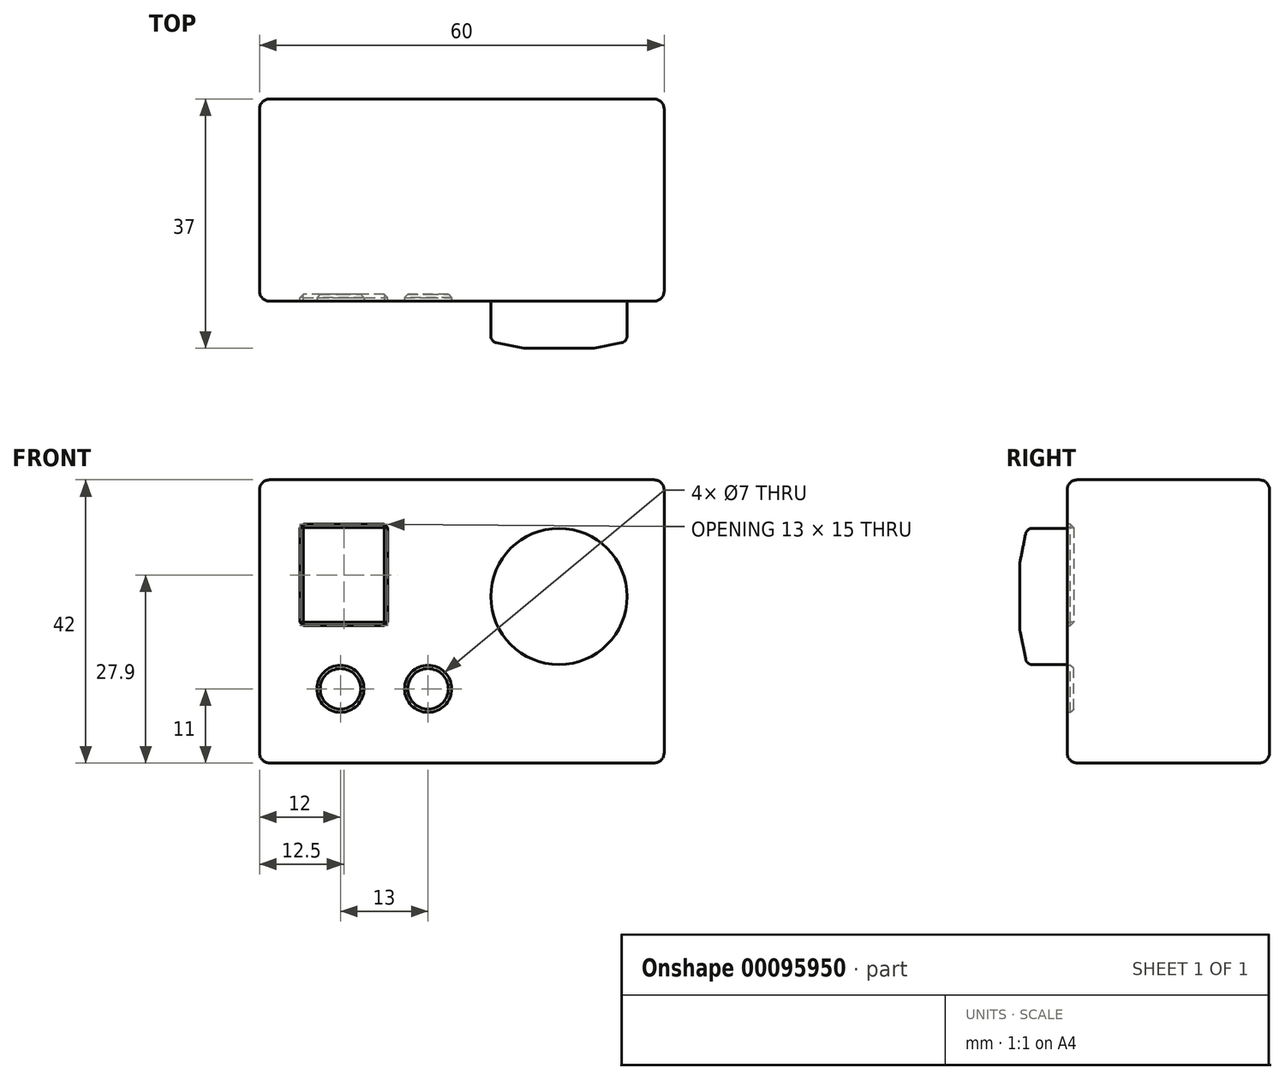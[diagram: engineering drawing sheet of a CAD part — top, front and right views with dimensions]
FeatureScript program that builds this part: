
annotation { "Feature Type Name" : "Feature", "Feature Type Description" : "" }
export const myFeature = defineFeature(function(context is Context, id is Id, definition is map)
    precondition{}
    {
        {
            var Q0;
            Q0=qCreatedBy(makeId("Front.planeOp"),FACE);
            var sketch = newSketch(context, id + "F0", { "sketchPlane" : qUnion([Q0])});
            skLineSegment(sketch, "E0.bottom", {"start": v(30, 21) * mm, "end": v(-30, 21) * mm});
            skLineSegment(sketch, "E0.top", {"start": v(30, -21) * mm, "end": v(-30, -21) * mm});
            skLineSegment(sketch, "E0.left", {"start": v(30, 21) * mm, "end": v(30, -21) * mm});
            skLineSegment(sketch, "E0.right", {"start": v(-30, 21) * mm, "end": v(-30, -21) * mm});
            skPoint(sketch, "E0.middle", {"position": v(0, 0) * mm});
            skSolve(sketch);
        }
        {
            var Q0;
            Q0 = qSketchRegion(id + "F0", true);
            extrude(context, id + "F1", {"entities" : qUnion([Q0]), "depth" : 30 * mm});
        }
        {
            var Q0;
            Q0=makeQuery(id+"F1.opExtrude","CAP_FACE",FACE,{"disambiguationData":[OSD([sQuery(id+"F0.wireOp",EDGE,"E0.bottom"),sQuery(id+"F0.wireOp",EDGE,"E0.top"),sQuery(id+"F0.wireOp",EDGE,"E0.left"),sQuery(id+"F0.wireOp",EDGE,"E0.right")])],"isStart":false});
            var sketch = newSketch(context, id + "F2", { "sketchPlane" : qUnion([Q0])});
            skCircle(sketch, "E1", {"center": v(-18, -10) * mm, "radius": 3.5 * mm});
            skCircle(sketch, "E2", {"center": v(-5, -10) * mm, "radius": 3.5 * mm});
            skLineSegment(sketch, "E3.bottom", {"start": v(-24, 14.4) * mm, "end": v(-11, 14.4) * mm});
            skLineSegment(sketch, "E3.top", {"start": v(-24, -0.6) * mm, "end": v(-11, -0.6) * mm});
            skLineSegment(sketch, "E3.left", {"start": v(-24, 14.4) * mm, "end": v(-24, -0.6) * mm});
            skLineSegment(sketch, "E3.right", {"start": v(-11, 14.4) * mm, "end": v(-11, -0.6) * mm});
            skSolve(sketch);
        }
        {
            var Q0;
            Q0 = qSketchRegion(id + "F2", true);
            extrude(context, id + "F3", {"entities" : qUnion([Q0]), "operationType" : NewBodyOperationType.REMOVE, "oppositeDirection" : true, "depth" : 1 * mm});
        }
        {
            var Q0;
            Q0=makeQuery(id+"F3.boolean.opBoolean","COPY",EDGE,{"derivedFrom":makeQuery(id+"F3.opExtrude","CAP_EDGE",EDGE,{"disambiguationData":[OSD([sQuery(id+"F2.wireOp",EDGE,"E1")])],"isStart":true})});
            var Q1;
            Q1=makeQuery(id+"F3.boolean.opBoolean","COPY",EDGE,{"derivedFrom":makeQuery(id+"F3.opExtrude","CAP_EDGE",EDGE,{"disambiguationData":[OSD([sQuery(id+"F2.wireOp",EDGE,"E2")])],"isStart":true})});
            var Q2;
            Q2=makeQuery(id+"F3.boolean.opBoolean","COPY",EDGE,{"derivedFrom":makeQuery(id+"F3.opExtrude","CAP_EDGE",EDGE,{"disambiguationData":[OSD([sQuery(id+"F2.wireOp",EDGE,"E3.right")])],"isStart":true})});
            var Q3;
            Q3=makeQuery(id+"F3.boolean.opBoolean","COPY",EDGE,{"derivedFrom":makeQuery(id+"F3.opExtrude","CAP_EDGE",EDGE,{"disambiguationData":[OSD([sQuery(id+"F2.wireOp",EDGE,"E1")])],"isStart":false})});
            var Q4;
            Q4=makeQuery(id+"F3.boolean.opBoolean","COPY",EDGE,{"derivedFrom":makeQuery(id+"F3.opExtrude","CAP_EDGE",EDGE,{"disambiguationData":[OSD([sQuery(id+"F2.wireOp",EDGE,"E2")])],"isStart":false})});
            var Q5;
            Q5=makeQuery(id+"F3.boolean.opBoolean","COPY",EDGE,{"derivedFrom":makeQuery(id+"F3.opExtrude","CAP_EDGE",EDGE,{"disambiguationData":[OSD([sQuery(id+"F2.wireOp",EDGE,"E3.bottom")])],"isStart":true})});
            var Q6;
            Q6=makeQuery(id+"F3.boolean.opBoolean","COPY",EDGE,{"derivedFrom":makeQuery(id+"F3.opExtrude","CAP_EDGE",EDGE,{"disambiguationData":[OSD([sQuery(id+"F2.wireOp",EDGE,"E3.top")])],"isStart":true})});
            var Q7;
            Q7=makeQuery(id+"F3.boolean.opBoolean","COPY",EDGE,{"derivedFrom":makeQuery(id+"F3.opExtrude","CAP_EDGE",EDGE,{"disambiguationData":[OSD([sQuery(id+"F2.wireOp",EDGE,"E3.left")])],"isStart":true})});
            var Q8;
            Q8=makeQuery(id+"F3.boolean.opBoolean","COPY",EDGE,{"derivedFrom":makeQuery(id+"F3.opExtrude","CAP_EDGE",EDGE,{"disambiguationData":[OSD([sQuery(id+"F2.wireOp",EDGE,"E3.left")])],"isStart":false})});
            var Q9;
            Q9=makeQuery(id+"F3.boolean.opBoolean","COPY",EDGE,{"derivedFrom":makeQuery(id+"F3.opExtrude","CAP_EDGE",EDGE,{"disambiguationData":[OSD([sQuery(id+"F2.wireOp",EDGE,"E3.right")])],"isStart":false})});
            var Q10;
            Q10=makeQuery(id+"F3.boolean.opBoolean","COPY",EDGE,{"derivedFrom":makeQuery(id+"F3.opExtrude","SWEPT_EDGE",EDGE,{"disambiguationData":[OSD([sQuery(id+"F2.wireOp",EDGE,"E3.bottom"),sQuery(id+"F2.wireOp",EDGE,"E3.left")])]})});
            var Q11;
            Q11=makeQuery(id+"F3.boolean.opBoolean","COPY",EDGE,{"derivedFrom":makeQuery(id+"F3.opExtrude","SWEPT_EDGE",EDGE,{"disambiguationData":[OSD([sQuery(id+"F2.wireOp",EDGE,"E3.bottom"),sQuery(id+"F2.wireOp",EDGE,"E3.right")])]})});
            var Q12;
            Q12=makeQuery(id+"F3.boolean.opBoolean","COPY",EDGE,{"derivedFrom":makeQuery(id+"F3.opExtrude","SWEPT_EDGE",EDGE,{"disambiguationData":[OSD([sQuery(id+"F2.wireOp",EDGE,"E3.top"),sQuery(id+"F2.wireOp",EDGE,"E3.left")])]})});
            var Q13;
            Q13=makeQuery(id+"F3.boolean.opBoolean","COPY",EDGE,{"derivedFrom":makeQuery(id+"F3.opExtrude","SWEPT_EDGE",EDGE,{"disambiguationData":[OSD([sQuery(id+"F2.wireOp",EDGE,"E3.top"),sQuery(id+"F2.wireOp",EDGE,"E3.right")])]})});
            var Q14;
            Q14=makeQuery(id+"F3.boolean.opBoolean","COPY",EDGE,{"derivedFrom":makeQuery(id+"F3.opExtrude","CAP_EDGE",EDGE,{"disambiguationData":[OSD([sQuery(id+"F2.wireOp",EDGE,"E3.bottom")])],"isStart":false})});
            var Q15;
            Q15=makeQuery(id+"F3.boolean.opBoolean","COPY",EDGE,{"derivedFrom":makeQuery(id+"F3.opExtrude","CAP_EDGE",EDGE,{"disambiguationData":[OSD([sQuery(id+"F2.wireOp",EDGE,"E3.top")])],"isStart":false})});
            chamfer(context, id + "F4", {"entities" : qUnion([Q0, Q1, Q2, Q3, Q4, Q5, Q6, Q7, Q8, Q9, Q10, Q11, Q12, Q13, Q14, Q15]), "width" : .5 * mm, "tangentPropagation" : true});
        }
        {
            var Q0;
            Q0=makeQuery(id+"F1.opExtrude","CAP_FACE",FACE,{"disambiguationData":[OSD([sQuery(id+"F0.wireOp",EDGE,"E0.bottom"),sQuery(id+"F0.wireOp",EDGE,"E0.top"),sQuery(id+"F0.wireOp",EDGE,"E0.left"),sQuery(id+"F0.wireOp",EDGE,"E0.right")])],"isStart":false});
            var sketch = newSketch(context, id + "F5", { "sketchPlane" : qUnion([Q0])});
            skCircle(sketch, "E4", {"center": v(14.4, 3.7) * mm, "radius": 10.1 * mm});
            skSolve(sketch);
        }
        {
            var Q0;
            Q0 = qSketchRegion(id + "F5", true);
            extrude(context, id + "F6", {"entities" : qUnion([Q0]), "operationType" : NewBodyOperationType.ADD, "depth" : 7 * mm});
        }
        {
            var Q0;
            Q0=makeQuery(id+"F6.opExtrude","CAP_EDGE",EDGE,{"disambiguationData":[OSD([sQuery(id+"F5.wireOp",EDGE,"E4")])],"isStart":false});
            chamfer(context, id + "F7", {"entities" : qUnion([Q0]), "chamferType" : ChamferType.TWO_OFFSETS, "width1" : 5 * mm, "oppositeDirection" : false, "width2" : 1 * mm, "tangentPropagation" : true});
        }
        {
            var Q0;
            {var subQ0=sQuery(id+"F5.wireOp",EDGE,"E4");Q0=makeQuery(id+"F7.opChamfer","BLEND_EDGE",EDGE,{"blendedFrom":[makeQuery(id+"F6.opExtrude","CAP_EDGE",EDGE,{"disambiguationData":[OSD([subQ0])],"isStart":false}),makeQuery(id+"F6.opExtrude","CAP_FACE",FACE,{"disambiguationData":[OSD([subQ0])],"isStart":false})],"blendedInto":[makeQuery(id+"F6.opExtrude","CAP_FACE",FACE,{"disambiguationData":[OSD([subQ0])],"isStart":false})]});}
            var Q1;
            {var subQ0=sQuery(id+"F5.wireOp",EDGE,"E4");Q1=makeQuery(id+"F7.opChamfer","BLEND_EDGE",EDGE,{"blendedFrom":[makeQuery(id+"F6.opExtrude","CAP_EDGE",EDGE,{"disambiguationData":[OSD([subQ0])],"isStart":false}),makeQuery(id+"F6.opExtrude","SWEPT_FACE",FACE,{"disambiguationData":[OSD([subQ0])]})],"blendedInto":[makeQuery(id+"F6.opExtrude","SWEPT_FACE",FACE,{"disambiguationData":[OSD([subQ0])]})]});}
            fillet(context, id + "F8", {"entities" : qUnion([Q0, Q1]), "radius" : 1 * mm, "tangentPropagation" : true, "allowEdgeOverflow" : false});
        }
        {
            var Q0;
            Q0=makeQuery(id+"F1.opExtrude","SWEPT_FACE",FACE,{"disambiguationData":[OSD([sQuery(id+"F0.wireOp",EDGE,"E0.bottom")])]});
            var Q1;
            Q1=makeQuery(id+"F1.opExtrude","SWEPT_FACE",FACE,{"disambiguationData":[OSD([sQuery(id+"F0.wireOp",EDGE,"E0.left")])]});
            var Q2;
            Q2=makeQuery(id+"F1.opExtrude","SWEPT_FACE",FACE,{"disambiguationData":[OSD([sQuery(id+"F0.wireOp",EDGE,"E0.top")])]});
            var Q3;
            Q3=makeQuery(id+"F1.opExtrude","SWEPT_FACE",FACE,{"disambiguationData":[OSD([sQuery(id+"F0.wireOp",EDGE,"E0.right")])]});
            fillet(context, id + "F9", {"entities" : qUnion([Q0, Q1, Q2, Q3]), "radius" : 1.5 * mm, "tangentPropagation" : true, "allowEdgeOverflow" : false});
        }
        {
            var Q0;
            Q0=makeQuery(id+"F1.opExtrude","SWEPT_BODY",BODY,{"disambiguationData":[OSD([sQuery(id+"F0.wireOp",EDGE,"E0.bottom"),sQuery(id+"F0.wireOp",EDGE,"E0.top"),sQuery(id+"F0.wireOp",EDGE,"E0.left"),sQuery(id+"F0.wireOp",EDGE,"E0.right")])]});
            transform(context, id + "F10", {"entities" : qUnion([Q0]), "transformType" : TransformType.TRANSLATION_3D, "dx" : 0 * mm, "dy" : 0 * mm, "dz" : 0 * mm, "makeCopy" : true});
        }
    });
